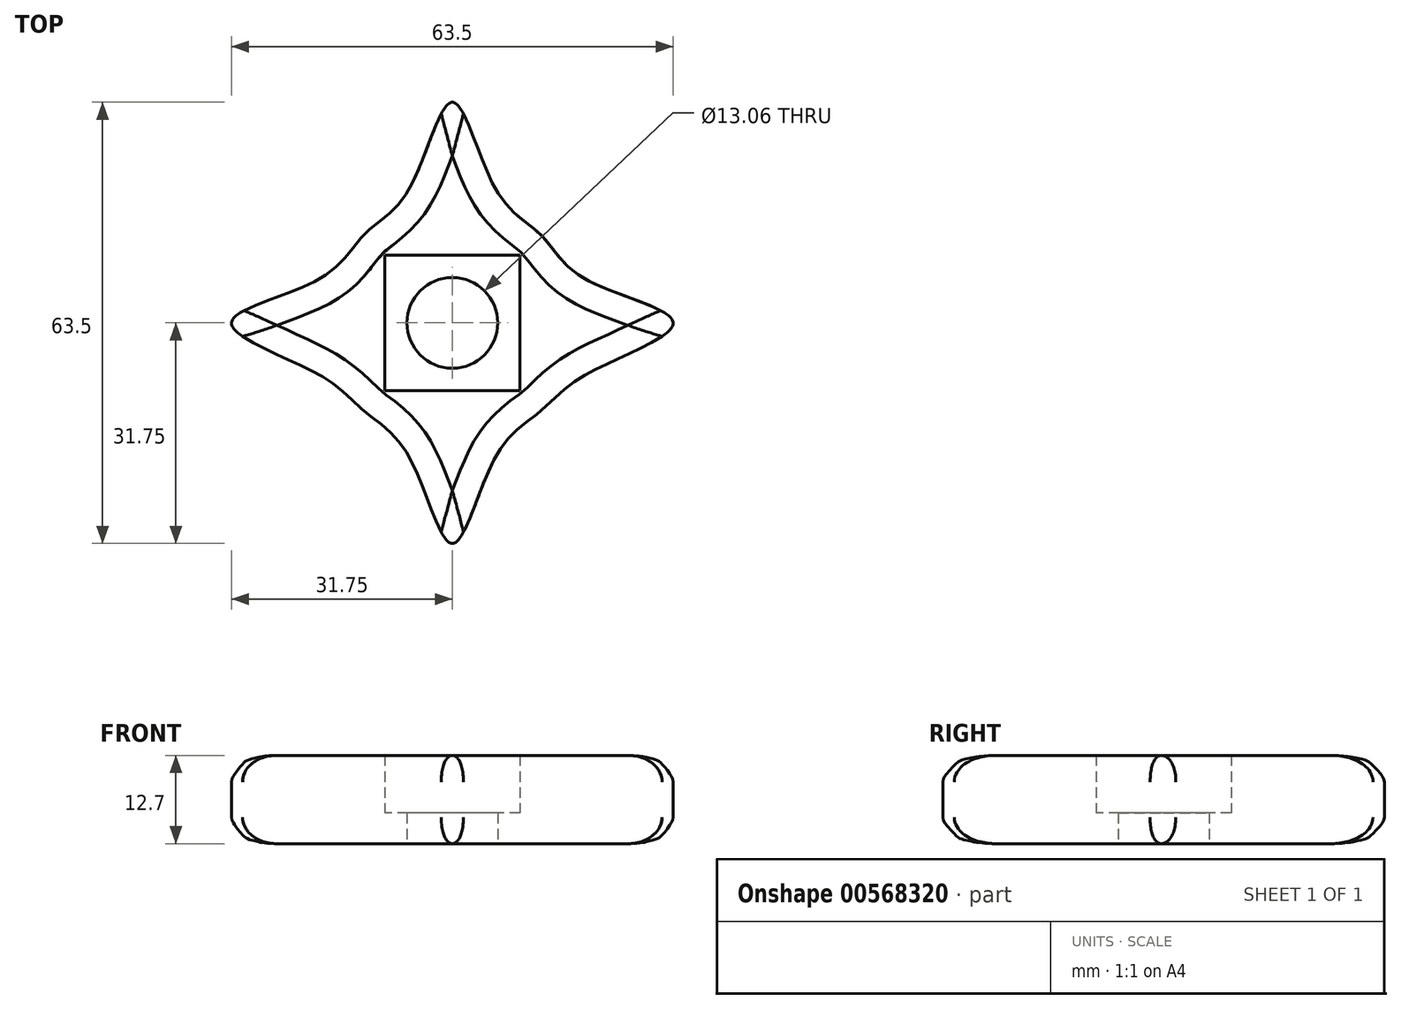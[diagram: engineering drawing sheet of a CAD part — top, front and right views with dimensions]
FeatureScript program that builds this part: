
annotation { "Feature Type Name" : "Feature", "Feature Type Description" : "" }
export const myFeature = defineFeature(function(context is Context, id is Id, definition is map)
    precondition{}
    {
        {
            var Q0;
            Q0=qCreatedBy(makeId("Top.planeOp"),FACE);
            var sketch = newSketch(context, id + "F0", { "sketchPlane" : qUnion([Q0])});
            skLineSegment(sketch, "E0.bottom", {"start": v(31.75, 31.75) * mm, "end": v(-31.75, 31.75) * mm, "construction": true});
            skLineSegment(sketch, "E0.top", {"start": v(31.75, -31.75) * mm, "end": v(-31.75, -31.75) * mm, "construction": true});
            skLineSegment(sketch, "E0.left", {"start": v(31.75, 31.75) * mm, "end": v(31.75, -31.75) * mm, "construction": true});
            skLineSegment(sketch, "E0.right", {"start": v(-31.75, 31.75) * mm, "end": v(-31.75, -31.75) * mm, "construction": true});
            skPoint(sketch, "E0.middle", {"position": v(0, 0) * mm});
            skLineSegment(sketch, "E1.bottom", {"start": v(9.73, 9.73) * mm, "end": v(-9.73, 9.73) * mm});
            skLineSegment(sketch, "E1.top", {"start": v(9.73, -9.73) * mm, "end": v(-9.73, -9.73) * mm});
            skLineSegment(sketch, "E1.left", {"start": v(9.73, 9.73) * mm, "end": v(9.73, -9.73) * mm});
            skLineSegment(sketch, "E1.right", {"start": v(-9.73, 9.73) * mm, "end": v(-9.73, -9.73) * mm});
            skLineSegment(sketch, "E2", {"start": v(-31.75, 31.75) * mm, "end": v(-12.7, 31.75) * mm});
            skLineSegment(sketch, "E3", {"start": v(-12.7, 31.75) * mm, "end": v(-12.7, -31.75) * mm, "construction": true});
            skLineSegment(sketch, "E4", {"start": v(31.75, 31.75) * mm, "end": v(12.7, 31.75) * mm});
            skLineSegment(sketch, "E5", {"start": v(12.7, 31.75) * mm, "end": v(12.7, -31.75) * mm, "construction": true});
            skLineSegment(sketch, "E6", {"start": v(-31.75, -31.75) * mm, "end": v(-31.75, -12.7) * mm});
            skLineSegment(sketch, "E7", {"start": v(-31.75, -12.7) * mm, "end": v(31.75, -12.7) * mm, "construction": true});
            skLineSegment(sketch, "E8", {"start": v(31.75, 31.75) * mm, "end": v(31.75, 12.7) * mm});
            skLineSegment(sketch, "E9", {"start": v(31.75, 12.7) * mm, "end": v(-31.75, 12.7) * mm, "construction": true});
            skLineSegment(sketch, "E10", {"start": v(-31.75, -32.94) * mm, "end": v(-31.75, -7.54) * mm});
            skLineSegment(sketch, "E11", {"start": v(-31.75, -7.54) * mm, "end": v(31.75, -7.54) * mm, "construction": true});
            skLineSegment(sketch, "E12", {"start": v(-31.75, 31.75) * mm, "end": v(-6.35, 31.75) * mm});
            skLineSegment(sketch, "E13", {"start": v(-6.35, 31.75) * mm, "end": v(-6.35, -31.75) * mm, "construction": true});
            skLineSegment(sketch, "E14", {"start": v(31.75, 31.75) * mm, "end": v(6.35, 31.75) * mm});
            skLineSegment(sketch, "E15", {"start": v(6.35, 31.75) * mm, "end": v(6.35, -31.75) * mm, "construction": true});
            skLineSegment(sketch, "E16", {"start": v(-31.75, 31.75) * mm, "end": v(-31.75, 6.35) * mm});
            skLineSegment(sketch, "E17", {"start": v(-31.75, 6.35) * mm, "end": v(31.75, 6.35) * mm, "construction": true});
            skLineSegment(sketch, "E18", {"start": v(-31.75, 31.75) * mm, "end": v(-19.05, 31.75) * mm});
            skLineSegment(sketch, "E19", {"start": v(-19.05, 31.75) * mm, "end": v(-19.05, -31.75) * mm, "construction": true});
            skLineSegment(sketch, "E20", {"start": v(31.75, -31.75) * mm, "end": v(19.05, -31.75) * mm});
            skLineSegment(sketch, "E21", {"start": v(19.05, -31.75) * mm, "end": v(19.05, 31.75) * mm, "construction": true});
            skLineSegment(sketch, "E22", {"start": v(-31.75, -31.75) * mm, "end": v(-31.75, -19.05) * mm});
            skLineSegment(sketch, "E23", {"start": v(-31.75, -19.05) * mm, "end": v(31.75, -19.05) * mm, "construction": true});
            skLineSegment(sketch, "E24", {"start": v(-31.75, 31.75) * mm, "end": v(-31.75, 19.05) * mm});
            skLineSegment(sketch, "E25", {"start": v(-31.75, 19.05) * mm, "end": v(31.75, 19.05) * mm, "construction": true});
            skFitSpline(sketch, "E26", {"points": [v(-31.75, 0) * mm, v(-19.05, 6.35) * mm, v(-12.7, 12.7) * mm, v(-6.35, 19.05) * mm, v(0, 31.75) * mm, v(6.35, 19.05) * mm, v(12.7, 12.7) * mm, v(19.05, 6.35) * mm, v(31.75, 0) * mm, v(19.05, -7.54) * mm, v(12.7, -12.7) * mm, v(6.35, -19.05) * mm, v(0, -31.75) * mm, v(-6.35, -19.05) * mm, v(-12.7, -12.7) * mm, v(-19.05, -7.54) * mm, v(-31.75, 0) * mm]});
            skCircle(sketch, "E27", {"center": v(0, 0) * mm, "radius": 6.53 * mm});
            skSolve(sketch);
        }
        {
            var Q0;
            Q0=makeQuery(id+"F0.imprint","IMPRINT",FACE,{"disambiguationData":[TD([[makeQuery(id+"F0.imprint","IMPRINT",EDGE,{"derivedFrom":sQuery(id+"F0.wireOp",EDGE,"E1.bottom")}),-1.0]])]});
            extrude(context, id + "F1", {"entities" : qUnion([Q0]), "depth" : 12.7 * mm, "offsetDistance" : 25.4 * mm});
        }
        {
            var Q0;
            Q0=makeQuery(id+"F0.imprint","IMPRINT",FACE,{"disambiguationData":[TD([[makeQuery(id+"F0.imprint","IMPRINT",EDGE,{"derivedFrom":sQuery(id+"F0.wireOp",EDGE,"E1.bottom")}),1.0]])]});
            extrude(context, id + "F2", {"entities" : qUnion([Q0]), "operationType" : NewBodyOperationType.ADD, "depth" : 4.42 * mm, "offsetDistance" : 25.4 * mm});
        }
        {
            var Q0;
            Q0=makeQuery(id+"F1.opExtrude","CAP_EDGE",EDGE,{"disambiguationData":[OSD([sQuery(id+"F0.wireOp",EDGE,"E26")])],"isStart":false});
            fillet(context, id + "F3", {"entities" : qUnion([Q0]), "radius" : 3.8 * mm, "tangentPropagation" : true, "allowEdgeOverflow" : false});
        }
        {
            var Q0;
            Q0=makeQuery(id+"F1.opExtrude","CAP_EDGE",EDGE,{"disambiguationData":[OSD([sQuery(id+"F0.wireOp",EDGE,"E26")])],"isStart":true});
            fillet(context, id + "F4", {"entities" : qUnion([Q0]), "radius" : 3.8 * mm, "tangentPropagation" : true, "allowEdgeOverflow" : false});
        }
    });
